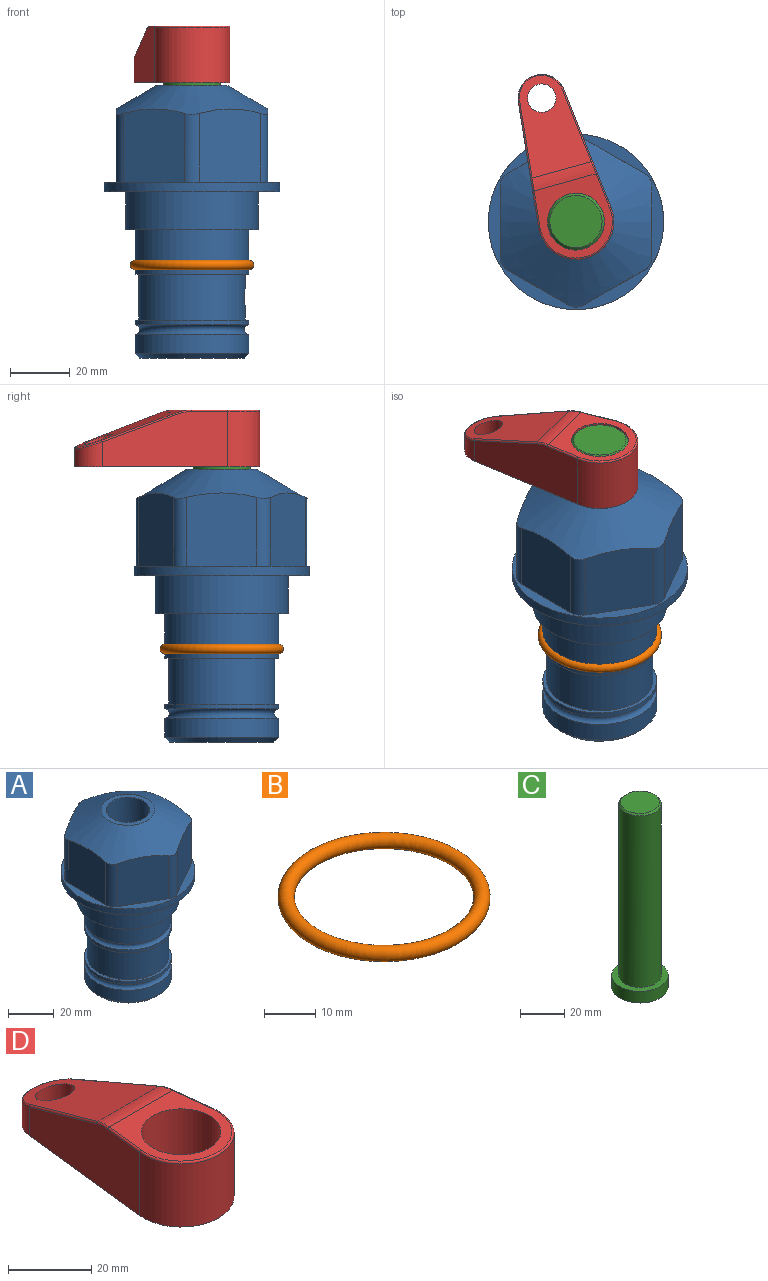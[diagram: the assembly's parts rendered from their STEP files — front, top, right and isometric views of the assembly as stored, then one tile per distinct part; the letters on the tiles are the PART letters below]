
ASSEMBLY  parts=4 mates=2
PART A: 36 faces, bbox 58.7x58.7x91.2 mm
  f0: cylinder r=17.78mm len=35.56mm, axis (0,0,1), area 1670.8mm2, adj f23,f24,f31
  f1: cylinder r=19.05mm len=38.1mm, axis (0,0,1), area 1191.9mm2, adj f26,f27,f30
  f2: plane 58.66x58.66mm, normal (0,0,-1), area 1150.6mm2, adj f3,f28
  f3: cylinder r=29.33mm len=58.66mm, axis (0,0,-1), area 585.1mm2, adj f2,f4
  f4: plane 58.66x58.66mm, normal (0,0,1), area 475.9mm2, adj f3,f5,f6,f7,f8,f9,f10,f11
  f5: plane 24.5x20.32mm, normal (-0.5,0.87,0), area 562.8mm2, adj f4,f15,f16,f17
  f6: plane 24.5x20.32mm, normal (0.5,0.87,0), area 562.8mm2, adj f4,f14,f15,f17
  f7: plane 24.5x23.48mm, normal (1,0,0), area 562.8mm2, adj f4,f13,f14,f17
  f8: plane 24.5x20.32mm, normal (0.5,-0.87,0), area 562.8mm2, adj f4,f12,f13,f17
  f9: plane 24.5x20.32mm, normal (-0.5,-0.87,0), area 562.8mm2, adj f4,f11,f12,f17
  f10: plane 24.5x23.48mm, normal (-1,0,0), area 562.8mm2, adj f4,f11,f16,f17
  f11: cylinder r=5.08mm len=23.01mm, axis (0,0,-1), area 121.2mm2, adj f4,f9,f10,f17
  f12: cylinder r=5.08mm len=23.01mm, axis (0,0,-1), area 121.2mm2, adj f4,f8,f9,f17
  f13: cylinder r=5.08mm len=23.01mm, axis (0,0,-1), area 121.2mm2, adj f4,f7,f8,f17
  f14: cylinder r=5.08mm len=23.01mm, axis (0,0,-1), area 121.2mm2, adj f4,f6,f7,f17
  f15: cylinder r=5.08mm len=23.01mm, axis (0,0,-1), area 121.2mm2, adj f4,f5,f6,f17
  f16: cylinder r=5.08mm len=23.01mm, axis (0,0,-1), area 121.2mm2, adj f4,f5,f10,f17
  f17: cone r=11.73mm half-angle=60deg, axis (0,0,-1), area 2071.8mm2, adj f5,f6,f7,f8,f9,f10,f11,f12
  f18: plane 23.46x23.46mm, normal (0,0,1), area 147.4mm2, adj f17,f35
  f19: plane 34.93x34.93mm, normal (0,0,-1), area 958mm2, adj f29
  f20: cylinder r=19.05mm len=38.1mm, axis (0,0,1), area 760.1mm2, adj f21,f29
  f21: torus R=19.05mm, axis (0,0,1), area 565.3mm2, adj f20,f22
  f22: cylinder r=19.05mm len=38.1mm, axis (0,0,1), area 190mm2, adj f21,f23
  f23: plane 38.1x38.1mm, normal (0,0,1), area 146.9mm2, adj f0,f22
  f24: plane 38.1x38.1mm, normal (0,0,-1), area 146.9mm2, adj f0,f25
  f25: cylinder r=19.05mm len=38.1mm, axis (0,0,1), area 190mm2, adj f24,f26
  f26: torus R=19.05mm, axis (0,0,1), area 565.3mm2, adj f1,f25
  f27: plane 44.45x44.45mm, normal (0,0,-1), area 411.7mm2, adj f1,f28
  f28: cylinder r=22.23mm len=44.45mm, axis (0,0,1), area 1773.5mm2, adj f2,f27
  f29: cone r=19.05mm half-angle=45deg, axis (0,0,1), area 257.5mm2, adj f19,f20
  f30: cylinder r=3.17mm len=6.75mm, axis (-1,0,0), area 128mm2, adj f1,f33
  f31: cylinder r=3.17mm len=6.35mm, axis (-1,0,0), area 102.5mm2, adj f0,f33
  f32: plane 25.4x25.4mm, normal (0,0,1), area 506.7mm2, adj f33
  f33: cylinder r=12.7mm len=66.42mm, axis (0,0,-1), area 5236.2mm2, adj f30,f31,f32,f34
  f34: cone r=9.53mm half-angle=30deg, axis (0,0,-1), area 443.4mm2, adj f33,f35
  f35: cylinder r=9.53mm len=19.05mm, axis (0,0,-1), area 849mm2, adj f18,f34
PART B: 1 faces, bbox 44.7x44.7x3.2 mm
  f0: torus R=19.05mm, axis (0,0,1), area 1193.9mm2
PART C: 6 faces, bbox 25.4x25.4x101.6 mm
  f0: plane 17.46x17.46mm, normal (0,0,1), area 239.5mm2, adj f5
  f1: plane 25.4x25.4mm, normal (0,0,-1), area 506.7mm2, adj f2
  f2: cylinder r=12.7mm len=25.4mm, axis (0,0,1), area 506.7mm2, adj f1,f3
  f3: plane 25.4x25.4mm, normal (0,0,1), area 221.7mm2, adj f2,f4
  f4: cylinder r=9.53mm len=94.46mm, axis (0,0,1), area 5653mm2, adj f3,f5
  f5: cone r=8.73mm half-angle=45deg, axis (0,0,-1), area 64.4mm2, adj f0,f4
PART D: 44 faces, bbox 27.5x64.5x19.1 mm
  f0: plane 2.3x0.95mm, normal (0,0,-1), area 1mm2, adj f25,f30,f34
  f1: plane 63.5x25.4mm, normal (0,0,-1), area 561.7mm2, adj f2,f3,f4,f5,f6,f7,f19,f20
  f2: cylinder r=12.7mm len=25.4mm, axis (0,0,-1), area 792.2mm2, adj f1,f3,f5,f13
  f3: plane 42.33x18.54mm, normal (0.99,0.11,0), area 647mm2, adj f1,f2,f4,f11,f12,f14
  f4: cylinder r=7.94mm len=15.78mm, axis (0,0,-1), area 158.6mm2, adj f1,f3,f5,f16
  f5: plane 42.33x18.54mm, normal (-0.99,0.11,0), area 647mm2, adj f1,f2,f4,f15,f17,f18
  f6: cylinder r=9.53mm len=19.05mm, axis (0,0,-1), area 1140.1mm2, adj f1,f8
  f7: cylinder r=4.76mm len=10.98mm, axis (0,0,-1), area 276.1mm2, adj f1,f9
  f8: plane 25.83x24.38mm, normal (0,0,1), area 262.2mm2, adj f6,f10,f11,f13,f15
  f9: plane 32.49x20.55mm, normal (0,0.34,0.94), area 489.9mm2, adj f7,f10,f14,f16,f18
  f10: cylinder r=12.7mm len=21.49mm, axis (-1,0,0), area 93.2mm2, adj f8,f9,f12,f17
  f11: cylinder r=0.51mm len=12.34mm, axis (0.11,-0.99,0), area 9.9mm2, adj f3,f8,f12,f13
  f12: bspline ~7.62x1.64mm, area 3.5mm2, adj f3,f10,f11,f14
  f13: torus R=12.19mm, axis (0,0,1), area 33.6mm2, adj f2,f8,f11,f15
  f14: cylinder r=0.51mm len=26.01mm, axis (0.1,-0.93,0.34), area 21.6mm2, adj f3,f9,f12,f16
  f15: cylinder r=0.51mm len=12.34mm, axis (0.11,0.99,0), area 9.9mm2, adj f5,f8,f13,f17
  f16: bspline ~15.78x7.05mm, area 15.7mm2, adj f4,f9,f14,f18
  f17: bspline ~7.62x1.64mm, area 3.5mm2, adj f5,f10,f15,f18
  f18: cylinder r=0.51mm len=26.01mm, axis (0.1,0.93,-0.34), area 21.6mm2, adj f5,f9,f16,f17
  f19: plane 21.6x14.29mm, normal (-0.99,-0.11,0), area 242.6mm2, adj f1,f26,f28,f34,f36,f38
  f20: plane 21.6x14.29mm, normal (0.99,-0.11,0), area 242.6mm2, adj f1,f27,f29,f37,f39,f41
  f21: cylinder r=12.7mm len=14.29mm, axis (0,0,-1), area 173.2mm2, adj f1,f26,f27,f30,f31,f33
  f22: cylinder r=7.94mm len=7.63mm, axis (0,0,-1), area 53.8mm2, adj f1,f28,f29,f42
  f23: plane 2.3x0.95mm, normal (0,0,-1), area 1mm2, adj f25,f33,f37
  f24: plane 17.94x12.32mm, normal (0,-0.34,-0.94), area 191.2mm2, adj f25,f38,f41,f42
  f25: cylinder r=9.53mm len=12.93mm, axis (-1,0,0), area 37.5mm2, adj f0,f23,f24,f31,f36,f39
  f26: cylinder r=1.59mm len=14.29mm, axis (0,0,-1), area 49mm2, adj f1,f19,f21,f32
  f27: cylinder r=1.59mm len=14.29mm, axis (0,0,-1), area 49mm2, adj f1,f20,f21,f35
  f28: cylinder r=1.59mm len=7.28mm, axis (0,0,-1), area 22.1mm2, adj f1,f19,f22,f40
  f29: cylinder r=1.59mm len=7.28mm, axis (0,0,-1), area 22.1mm2, adj f1,f20,f22,f43
  f30: torus R=14.29mm, axis (0,0,1), area 5.8mm2, adj f0,f21,f31,f32
  f31: bspline ~11.06x2.73mm, area 20.8mm2, adj f21,f25,f30,f33
  f32: sphere r=1.59mm, area 5.4mm2, adj f26,f30,f34
  f33: torus R=14.29mm, axis (0,0,1), area 5.8mm2, adj f21,f23,f31,f35
  f34: cylinder r=1.59mm len=1.68mm, axis (-0.11,0.99,0), area 2.4mm2, adj f0,f19,f32,f36
  f35: sphere r=1.59mm, area 5.4mm2, adj f27,f33,f37
  f36: bspline ~5.82x2.33mm, area 7.7mm2, adj f19,f25,f34,f38
  f37: cylinder r=1.59mm len=1.68mm, axis (0.11,0.99,0), area 2.4mm2, adj f20,f23,f35,f39
  f38: cylinder r=1.59mm len=18.33mm, axis (0.1,-0.93,0.34), area 46.7mm2, adj f19,f24,f36,f40
  f39: bspline ~5.82x2.33mm, area 7.7mm2, adj f20,f25,f37,f41
  f40: sphere r=1.59mm, area 3.6mm2, adj f28,f38,f42
  f41: cylinder r=1.59mm len=18.33mm, axis (0.1,0.93,-0.34), area 46.7mm2, adj f20,f24,f39,f43
  f42: bspline ~8.31x1.84mm, area 15.3mm2, adj f22,f24,f40,f43
  f43: sphere r=1.59mm, area 3.6mm2, adj f29,f41,f42
PLACE A at identity fixed
PLACE B at identity
PLACE C rot(axis=(0,0,1),15.5deg) t=(0,0,-18.25)mm
PLACE D rot(axis=(0,0,1),15.5deg) t=(0,0,36.36)mm
MATE cylindrical C.f2 <-> A.f0  axis (0,0,1) through (0,0,7.39)mm
MATE fastened D.f2 <-> C.f2  axis (0,0,-1) through (0,0,55.41)mm
